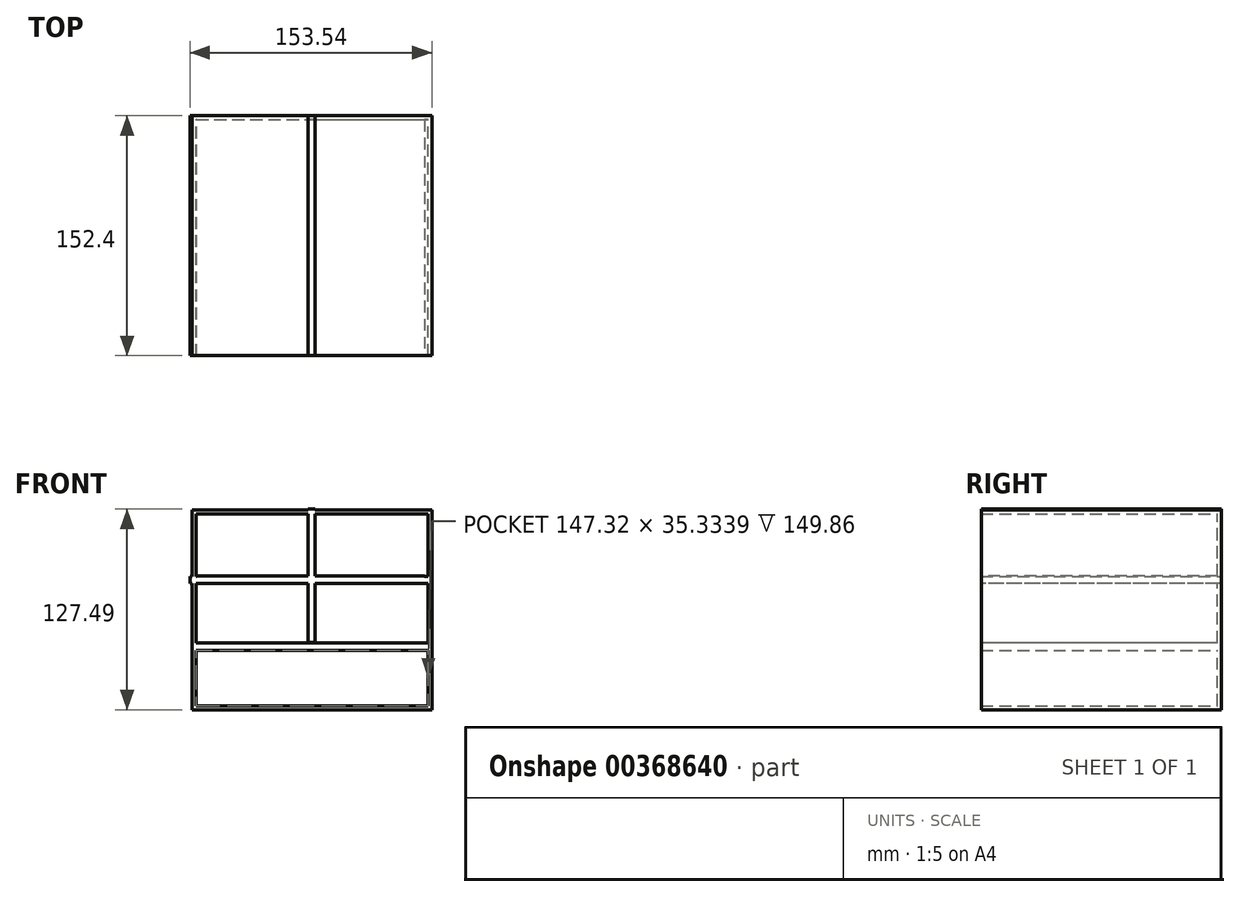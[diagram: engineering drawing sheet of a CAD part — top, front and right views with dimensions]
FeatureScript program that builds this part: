
annotation { "Feature Type Name" : "Feature", "Feature Type Description" : "" }
export const myFeature = defineFeature(function(context is Context, id is Id, definition is map)
    precondition{}
    {
        {
            var Q0;
            Q0=qCreatedBy(makeId("Front.planeOp"),FACE);
            var sketch = newSketch(context, id + "F0", { "sketchPlane" : qUnion([Q0])});
            skLineSegment(sketch, "E0.bottom", {"start": v(-116.91, -67.65) * mm, "end": v(35.49, -67.65) * mm});
            skLineSegment(sketch, "E0.top", {"start": v(-116.91, 59.35) * mm, "end": v(35.49, 59.35) * mm});
            skLineSegment(sketch, "E0.left", {"start": v(-116.91, -67.65) * mm, "end": v(-116.91, 59.35) * mm});
            skLineSegment(sketch, "E0.right", {"start": v(35.49, -67.65) * mm, "end": v(35.49, 59.35) * mm});
            skSolve(sketch);
        }
        {
            var Q0;
            Q0=makeQuery(id+"F0.imprint","IMPRINT",FACE,{"disambiguationData":[TD([[makeQuery(id+"F0.imprint","IMPRINT",EDGE,{"derivedFrom":sQuery(id+"F0.wireOp",EDGE,"E0.bottom")}),1.0]])]});
            extrude(context, id + "F1", {"entities" : qUnion([Q0]), "depth" : 152.4 * mm});
        }
        {
            var Q0;
            Q0=makeQuery(id+"F1.opExtrude","CAP_FACE",FACE,{"disambiguationData":[OSD([sQuery(id+"F0.wireOp",EDGE,"E0.bottom"),sQuery(id+"F0.wireOp",EDGE,"E0.top"),sQuery(id+"F0.wireOp",EDGE,"E0.left"),sQuery(id+"F0.wireOp",EDGE,"E0.right")])],"isStart":false});
            shell(context, id + "F2", {"entities" : qUnion([Q0]), "thickness" : 2.54 * mm});
        }
        {
            var Q0;
            Q0=qCreatedBy(makeId("Front.planeOp"),FACE);
            var sketch = newSketch(context, id + "F3", { "sketchPlane" : qUnion([Q0])});
            skLineSegment(sketch, "E1", {"start": v(30.82, 17.44) * mm, "end": v(-113.96, 17.44) * mm});
            skLineSegment(sketch, "E2", {"start": v(34.97, -25.02) * mm, "end": v(-114.9, -25.02) * mm});
            skLineSegment(sketch, "E3", {"start": v(-113.96, 17.44) * mm, "end": v(-113.96, 12.8) * mm});
            skLineSegment(sketch, "E4", {"start": v(-113.96, 12.8) * mm, "end": v(30.82, 12.8) * mm});
            skLineSegment(sketch, "E5", {"start": v(-114.9, -25.02) * mm, "end": v(-114.9, -29.77) * mm});
            skLineSegment(sketch, "E6", {"start": v(-114.9, -29.77) * mm, "end": v(34.97, -29.77) * mm});
            skLineSegment(sketch, "E7", {"start": v(34.97, -29.77) * mm, "end": v(34.97, -25.02) * mm});
            skLineSegment(sketch, "E8", {"start": v(30.82, 17.44) * mm, "end": v(30.82, 12.8) * mm});
            skSolve(sketch);
        }
        {
            var Q0;
            Q0 = qSketchRegion(id + "F3", true);
            extrude(context, id + "F4", {"entities" : qUnion([Q0]), "operationType" : NewBodyOperationType.ADD, "depth" : 152.4 * mm});
        }
        {
            var Q0;
            Q0=qCreatedBy(makeId("Front.planeOp"),FACE);
            var sketch = newSketch(context, id + "F5", { "sketchPlane" : qUnion([Q0])});
            skLineSegment(sketch, "E9", {"start": v(-118.05, 17.05) * mm, "end": v(34.35, 17.05) * mm});
            skLineSegment(sketch, "E10", {"start": v(34.35, 17.05) * mm, "end": v(34.35, 12.7) * mm});
            skLineSegment(sketch, "E11", {"start": v(34.35, 12.7) * mm, "end": v(-118.05, 12.7) * mm});
            skLineSegment(sketch, "E12", {"start": v(-118.05, 12.7) * mm, "end": v(-118.05, 17.05) * mm});
            skSolve(sketch);
        }
        {
            var Q0;
            Q0 = qSketchRegion(id + "F5", true);
            extrude(context, id + "F6", {"entities" : qUnion([Q0]), "operationType" : NewBodyOperationType.ADD, "depth" : 152.4 * mm});
        }
        {
            var Q0;
            Q0=qCreatedBy(makeId("Front.planeOp"),FACE);
            var sketch = newSketch(context, id + "F7", { "sketchPlane" : qUnion([Q0])});
            skLineSegment(sketch, "E13", {"start": v(-41.03, 59.84) * mm, "end": v(-38.86, 59.84) * mm});
            skLineSegment(sketch, "E14", {"start": v(-38.86, 59.84) * mm, "end": v(-38.86, -24.94) * mm});
            skLineSegment(sketch, "E15.MirrorCS", {"start": v(-43.2, 59.84) * mm, "end": v(-43.2, -24.94) * mm});
            skLineSegment(sketch, "E16", {"start": v(-43.2, 59.84) * mm, "end": v(-38.86, 59.84) * mm});
            skLineSegment(sketch, "E17", {"start": v(-43.2, -24.94) * mm, "end": v(-38.86, -24.94) * mm});
            skSolve(sketch);
        }
        {
            var Q0;
            Q0 = qSketchRegion(id + "F7", true);
            extrude(context, id + "F8", {"entities" : qUnion([Q0]), "operationType" : NewBodyOperationType.ADD, "depth" : 152.4 * mm});
        }
    });
